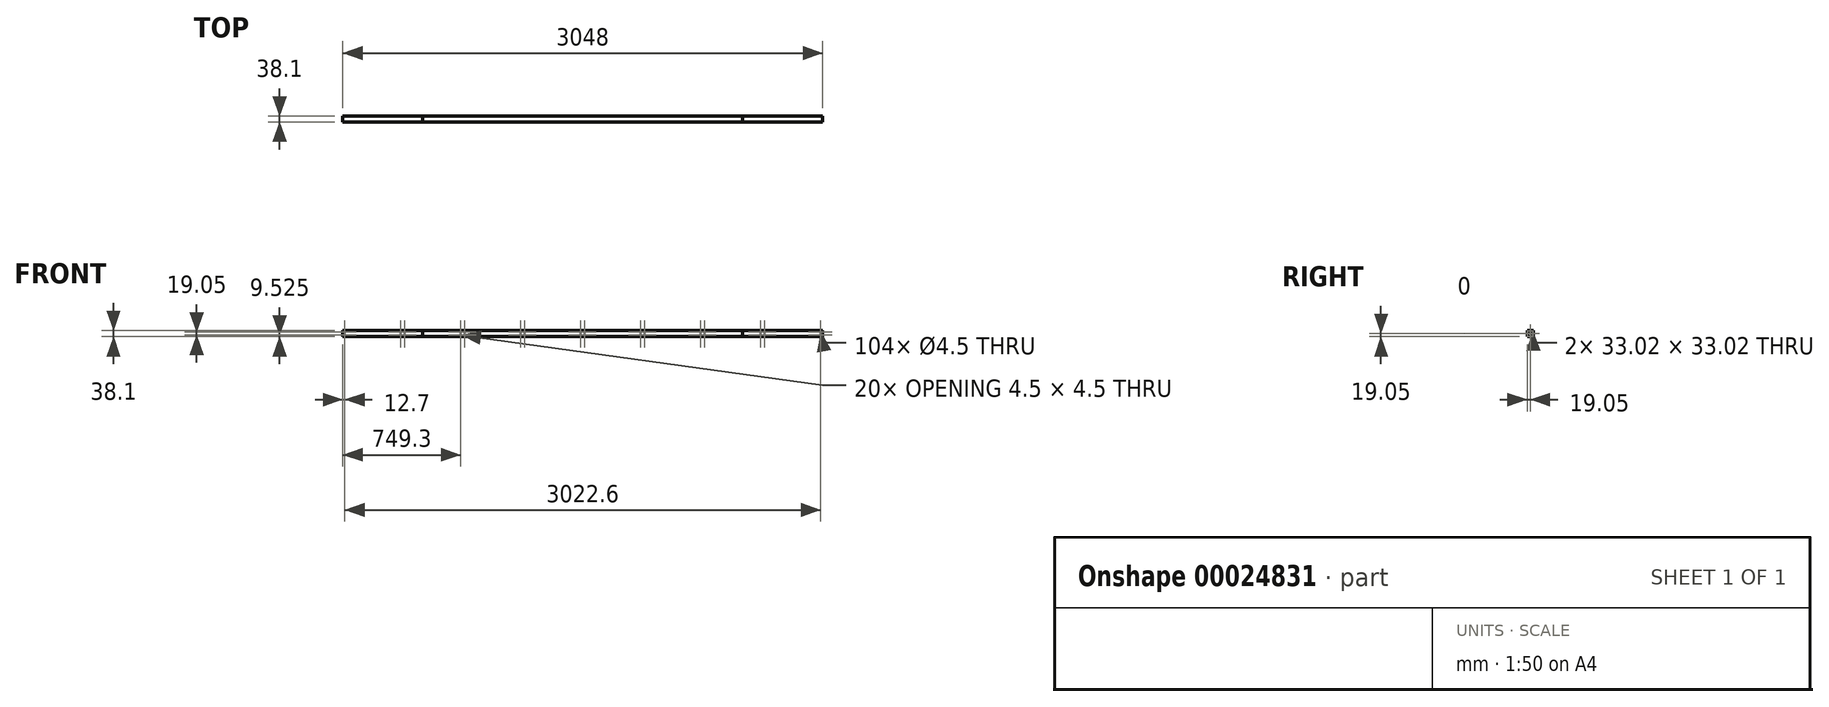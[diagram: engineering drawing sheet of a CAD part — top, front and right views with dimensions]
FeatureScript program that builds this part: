
annotation { "Feature Type Name" : "Feature", "Feature Type Description" : "" }
export const myFeature = defineFeature(function(context is Context, id is Id, definition is map)
    precondition{}
    {
        {
            var Q0;
            Q0=qCreatedBy(makeId("Right.planeOp"),FACE);
            var sketch = newSketch(context, id + "F0", { "sketchPlane" : qUnion([Q0])});
            skLineSegment(sketch, "E0.rect.bottom", {"start": v(-19.05, 19.05) * mm, "end": v(19.05, 19.05) * mm});
            skLineSegment(sketch, "E0.rect.top", {"start": v(-19.05, -19.05) * mm, "end": v(19.05, -19.05) * mm});
            skLineSegment(sketch, "E0.rect.left", {"start": v(-19.05, 19.05) * mm, "end": v(-19.05, -19.05) * mm});
            skLineSegment(sketch, "E0.rect.right", {"start": v(19.05, 19.05) * mm, "end": v(19.05, -19.05) * mm});
            skPoint(sketch, "E0.rect.middle", {"position": v(0, 0) * mm});
            skLineSegment(sketch, "E1.rect.bottom", {"start": v(-16.5, 16.5) * mm, "end": v(16.51, 16.5) * mm});
            skLineSegment(sketch, "E1.rect.top", {"start": v(-16.51, -16.51) * mm, "end": v(16.5, -16.51) * mm});
            skLineSegment(sketch, "E1.rect.left", {"start": v(-16.5, 16.5) * mm, "end": v(-16.51, -16.51) * mm});
            skLineSegment(sketch, "E1.rect.right", {"start": v(16.51, 16.5) * mm, "end": v(16.5, -16.51) * mm});
            skSolve(sketch);
        }
        {
            var Q0;
            Q0=makeQuery(id+"F0.imprint","IMPRINT",FACE,{"disambiguationData":[TD([[makeQuery(id+"F0.imprint","IMPRINT",EDGE,{"derivedFrom":sQuery(id+"F0.wireOp",EDGE,"E0.rect.bottom")}),-1.0]])]});
            extrude(context, id + "F1", {"entities" : qUnion([Q0]), "endBound" : BoundingType.SYMMETRIC, "depth" : 3048 * mm});
        }
        {
            var Q0;
            Q0=makeQuery(id+"F0.imprint","IMPRINT",FACE,{"disambiguationData":[TD([[makeQuery(id+"F0.imprint","IMPRINT",EDGE,{"derivedFrom":sQuery(id+"F0.wireOp",EDGE,"E0.rect.bottom")}),-1.0]])]});
            extrude(context, id + "F2", {"entities" : qUnion([Q0]), "endBound" : BoundingType.SYMMETRIC, "depth" : 2032 * mm});
        }
        {
            var Q0;
            Q0=makeQuery(id+"F1.opExtrude","SWEPT_FACE",FACE,{"disambiguationData":[OSD([sQuery(id+"F0.wireOp",EDGE,"E0.rect.left")])]});
            var sketch = newSketch(context, id + "F3", { "sketchPlane" : qUnion([Q0])});
            skLineSegment(sketch, "E2.rect.bottom", {"start": v(-12.7, 9.52) * mm, "end": v(12.7, 9.52) * mm, "construction": true});
            skLineSegment(sketch, "E2.rect.top", {"start": v(-12.7, -9.52) * mm, "end": v(12.7, -9.52) * mm, "construction": true});
            skLineSegment(sketch, "E2.rect.left", {"start": v(-12.7, 9.53) * mm, "end": v(-12.7, -9.52) * mm, "construction": true});
            skLineSegment(sketch, "E2.rect.right", {"start": v(12.7, 9.52) * mm, "end": v(12.7, -9.52) * mm, "construction": true});
            skPoint(sketch, "E2.rect.middle", {"position": v(0, 0) * mm});
            skCircle(sketch, "E3", {"center": v(-12.7, 9.53) * mm, "radius": 2.25 * mm});
            skCircle(sketch, "E4", {"center": v(12.7, 9.52) * mm, "radius": 2.25 * mm});
            skCircle(sketch, "E5", {"center": v(-12.7, -9.52) * mm, "radius": 2.25 * mm});
            skCircle(sketch, "E6", {"center": v(12.7, -9.52) * mm, "radius": 2.25 * mm});
            skCircle(sketch, "E7.1.0.0", {"center": v(368.3, -9.52) * mm, "radius": 2.25 * mm});
            skCircle(sketch, "E7.1.0.1", {"center": v(368.3, 9.53) * mm, "radius": 2.25 * mm});
            skCircle(sketch, "E7.1.0.2", {"center": v(393.7, 9.53) * mm, "radius": 2.25 * mm});
            skCircle(sketch, "E7.1.0.3", {"center": v(393.7, -9.52) * mm, "radius": 2.25 * mm});
            skCircle(sketch, "E7.2.0.0", {"center": v(749.3, -9.52) * mm, "radius": 2.25 * mm});
            skCircle(sketch, "E7.2.0.1", {"center": v(749.3, 9.53) * mm, "radius": 2.25 * mm});
            skCircle(sketch, "E7.2.0.2", {"center": v(774.7, 9.53) * mm, "radius": 2.25 * mm});
            skCircle(sketch, "E7.2.0.3", {"center": v(774.7, -9.52) * mm, "radius": 2.25 * mm});
            skCircle(sketch, "E7.3.0.0", {"center": v(1130.3, -9.52) * mm, "radius": 2.25 * mm});
            skCircle(sketch, "E7.3.0.1", {"center": v(1130.3, 9.53) * mm, "radius": 2.25 * mm});
            skCircle(sketch, "E7.3.0.2", {"center": v(1155.7, 9.53) * mm, "radius": 2.25 * mm});
            skCircle(sketch, "E7.3.0.3", {"center": v(1155.7, -9.52) * mm, "radius": 2.25 * mm});
            skCircle(sketch, "E7.4.0.0", {"center": v(1511.3, -9.52) * mm, "radius": 2.25 * mm});
            skCircle(sketch, "E7.4.0.1", {"center": v(1511.3, 9.53) * mm, "radius": 2.25 * mm});
            skCircle(sketch, "E7.4.0.2", {"center": v(1536.7, 9.53) * mm, "radius": 2.25 * mm});
            skCircle(sketch, "E7.4.0.3", {"center": v(1536.7, -9.52) * mm, "radius": 2.25 * mm});
            skLineSegment(sketch, "E7.direction1", {"start": v(-12.7, -9.52) * mm, "end": v(368.3, -9.52) * mm, "construction": true});
            skCircle(sketch, "E8.1.0.0", {"center": v(-393.7, -9.52) * mm, "radius": 2.25 * mm});
            skCircle(sketch, "E8.1.0.1", {"center": v(-393.7, 9.53) * mm, "radius": 2.25 * mm});
            skCircle(sketch, "E8.1.0.2", {"center": v(-368.3, 9.53) * mm, "radius": 2.25 * mm});
            skCircle(sketch, "E8.1.0.3", {"center": v(-368.3, -9.52) * mm, "radius": 2.25 * mm});
            skCircle(sketch, "E8.2.0.0", {"center": v(-774.7, -9.52) * mm, "radius": 2.25 * mm});
            skCircle(sketch, "E8.2.0.1", {"center": v(-774.7, 9.53) * mm, "radius": 2.25 * mm});
            skCircle(sketch, "E8.2.0.2", {"center": v(-749.3, 9.53) * mm, "radius": 2.25 * mm});
            skCircle(sketch, "E8.2.0.3", {"center": v(-749.3, -9.52) * mm, "radius": 2.25 * mm});
            skCircle(sketch, "E8.3.0.0", {"center": v(-1155.7, -9.52) * mm, "radius": 2.25 * mm});
            skCircle(sketch, "E8.3.0.1", {"center": v(-1155.7, 9.53) * mm, "radius": 2.25 * mm});
            skCircle(sketch, "E8.3.0.2", {"center": v(-1130.3, 9.53) * mm, "radius": 2.25 * mm});
            skCircle(sketch, "E8.3.0.3", {"center": v(-1130.3, -9.52) * mm, "radius": 2.25 * mm});
            skLineSegment(sketch, "E8.direction1", {"start": v(-12.7, -9.52) * mm, "end": v(-393.7, -9.52) * mm, "construction": true});
            skCircle(sketch, "E9.0.4.0", {"center": v(-1536.7, -9.52) * mm, "radius": 2.25 * mm});
            skCircle(sketch, "E9.2.4.0", {"center": v(-1536.7, 9.53) * mm, "radius": 2.25 * mm});
            skCircle(sketch, "E9.4.4.0", {"center": v(-1511.3, 9.52) * mm, "radius": 2.25 * mm});
            skCircle(sketch, "E9.6.4.0", {"center": v(-1511.3, -9.52) * mm, "radius": 2.25 * mm});
            skSolve(sketch);
        }
        {
            var Q0;
            Q0 = qSketchRegion(id + "F3", true);
            var Q1;
            Q1=makeQuery(id+"F1.opExtrude","SWEPT_FACE",FACE,{"disambiguationData":[OSD([sQuery(id+"F0.wireOp",EDGE,"E0.rect.right")])]});
            extrude(context, id + "F4", {"entities" : qUnion([Q0]), "operationType" : NewBodyOperationType.REMOVE, "endBound" : BoundingType.UP_TO_SURFACE, "oppositeDirection" : true, "endBoundEntityFace" : qUnion([Q1]), "depth" : 25.4 * mm});
        }
    });
